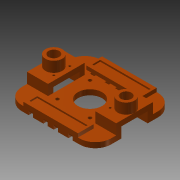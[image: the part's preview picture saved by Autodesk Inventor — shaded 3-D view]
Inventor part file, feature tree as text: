
AUTODESK INVENTOR PART (.ipt)
format: ipt  version: 2013 (Build 170138000, 138)  size: 325,632 bytes
history: native  units: mm
features: extrude x12, sketch x12, mirror x3, fillet x2, projected_geometry x1
ambient origin geometry x8: Origin, YZ Plane, XZ Plane, XY Plane, X Axis, Y Axis, Z Axis, Center Point
bodies: Solid1 (feature_tree)
feature tree (30):
  extrude  "Extrusion1"  Depth=75.0mm
  extrude  "Extrusion2"  Depth=3.2mm
  extrude  "Extrusion3"  Depth=23.0mm
  extrude  "Extrusion4"  Depth=15.0mm
  extrude  "Extrusion15"  Depth=10.0mm
  extrude  "Extrusion16"  Depth=48.0mm TaperAngle=0.0deg
  fillet  "Fillet6"  Radius=2.0mm
  mirror  "Mirror1"
  extrude  "Extrusion6"  Depth=35.0mm
  mirror  "Mirror2"
  extrude  "Extrusion7"  Depth=20.0mm TaperAngle=0.0deg
  extrude  "Extrusion8"  Depth=25.0mm
  extrude  "Extrusion9"  Depth=10.1mm
  extrude  "Extrusion10"  Depth=20.0mm TaperAngle=0.0deg
  extrude  "Extrusion14"  Depth=15.266mm
  mirror  "Mirror3"
  fillet  "Fillet5"  Radius=2.0mm
  sketch  "Sketch1"  dims[d0=85.0mm d3=75.0mm]
  sketch  "Sketch2"  dims[d4=5.0mm d5=0.0mm d6=3.2mm]
  sketch  "Sketch3"  dims[d8=31.0mm d9=23.0mm]
  sketch  "Sketch4"  dims[d10=5.0mm d11=0.0mm d12=15.0mm]
  sketch  "Sketch6"  dims[d14=7.5mm d15=10.0mm]
  sketch  "Sketch7"  dims[d16=7.5mm d17=48.0mm d18=0.0mm d19=2.0mm d20=0.0mm]
  sketch  "Sketch8"  dims[d29=1.5mm d30=0.0mm d31=35.0mm]
  sketch  "Sketch9"  dims[d33=20.0mm d34=20.0mm d35=0.0mm]
  sketch  "Sketch10"  dims[d36=10.0mm d38=25.0mm]
  sketch  "Sketch14"  dims[d39=20.0mm d40=0.0mm d41=10.1mm]
  sketch  "Sketch15"  dims[d43=8.0mm d44=20.0mm d45=0.0mm]
  sketch  "Sketch16"  dims[d46=7.6333mm d47=15.266mm d48=2.0mm d49=20.0mm d50=0.0mm d68=15.0mm d69=16.0mm d71=10.0mm d72=0.0mm d73=19.0mm d74=5.0mm d75=4.0mm d76=1.5mm d77=10.0mm d78=0.0mm d79=2.0mm d80=0.0mm d81=2.0mm]
  projected_geometry  "Project Cut Edges1"
